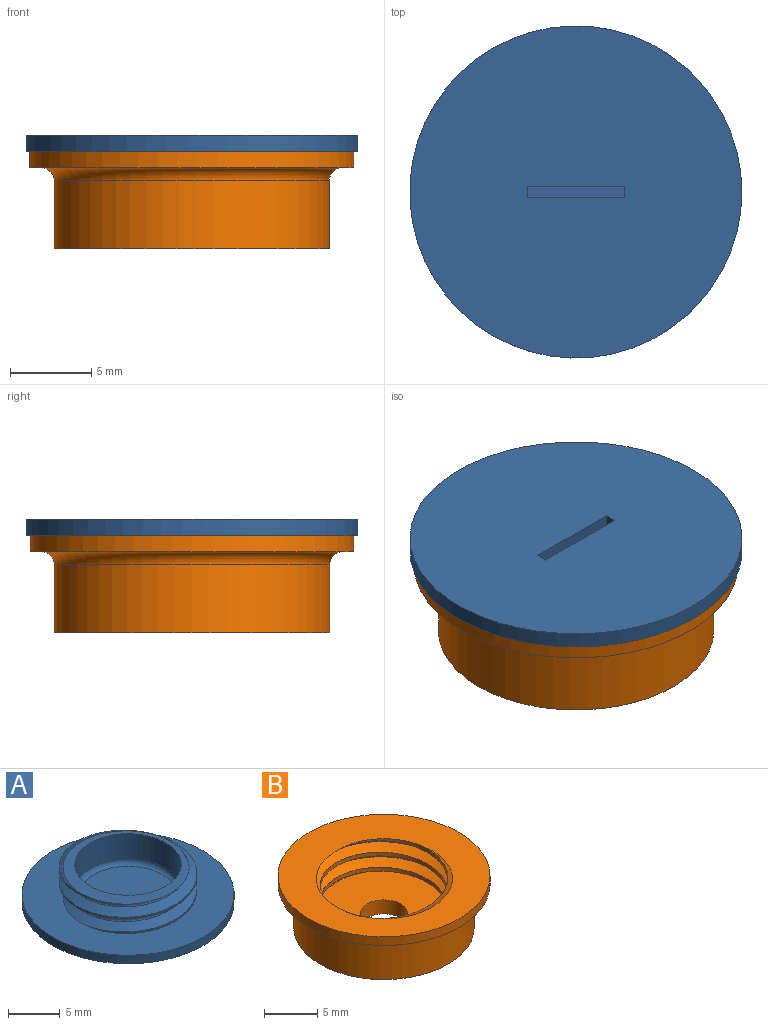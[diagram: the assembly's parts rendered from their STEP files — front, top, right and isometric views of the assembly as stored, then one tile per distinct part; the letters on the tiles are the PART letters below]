
ASSEMBLY  parts=2 mates=1
PART A: 16 faces, bbox 21x21x5.7 mm
  f0: plane 20.5x20.5mm, normal (0,0,-1), area 325.9mm2, adj f1,f11,f12,f13,f14
  f1: cylinder r=10.25mm len=20.5mm, axis (0,0,-1), area 64.4mm2, adj f0,f2
  f2: plane 20.99x20.99mm, normal (0,0,1), area 212.7mm2, adj f1,f4,f7,f8,f9
  f3: cylinder r=5.15mm len=10.3mm, axis (0,0,-1), area 97.1mm2, adj f5,f10
  f4: cylinder r=6.65mm len=13.3mm, axis (0,0,-1), area 18.3mm2, adj f2,f5,f8,f9
  f5: plane 12.77x12.71mm, normal (0,0,1), area 34.1mm2, adj f3,f4,f7,f8,f9
  f6: plane 9.3x9.3mm, normal (0,0,1), area 67.9mm2, adj f10
  f7: bspline ~13.17x11.41mm, area 34.7mm2, adj f2,f5,f8,f9
  f8: bspline ~15.36x13.3mm, area 85mm2, adj f2,f4,f5,f7
  f9: bspline ~15.36x13.3mm, area 85mm2, adj f2,f4,f5,f7
  f10: torus R=4.65mm, axis (0,0,1), area 24.5mm2, adj f3,f6
  f11: plane 0.8x0.7mm, normal (-1,0,0), area 0.6mm2, adj f0,f12,f14,f15
  f12: plane 6x0.8mm, normal (0,1,0), area 4.8mm2, adj f0,f11,f13,f15
  f13: plane 0.8x0.7mm, normal (1,0,0), area 0.6mm2, adj f0,f12,f14,f15
  f14: plane 6x0.8mm, normal (0,-1,0), area 4.8mm2, adj f0,f11,f13,f15
  f15: plane 6x0.7mm, normal (0,0,-1), area 4.2mm2, adj f11,f12,f13,f14
PART B: 12 faces, bbox 21.9x21.9x7.3 mm
  f0: plane 17x17mm, normal (0,0,-1), area 211.1mm2, adj f5,f6
  f1: plane 13.35x13.34mm, normal (0,0,1), area 115mm2, adj f6,f7,f8,f9,f10
  f2: plane 20.54x20.54mm, normal (0,0,1), area 183.3mm2, adj f3,f7,f8,f9,f10
  f3: cylinder r=10mm len=20mm, axis (0,0,-1), area 62.8mm2, adj f2,f4
  f4: plane 20x20mm, normal (0,0,-1), area 42.4mm2, adj f3,f11
  f5: cylinder r=8.5mm len=17mm, axis (0,0,-1), area 224.3mm2, adj f0,f11
  f6: cylinder r=2.25mm len=4.5mm, axis (0,0,-1), area 22.6mm2, adj f0,f1
  f7: bspline ~16.1x13.94mm, area 112.5mm2, adj f1,f2,f9,f10
  f8: bspline ~16.1x13.94mm, area 112.3mm2, adj f1,f2,f9,f10
  f9: bspline ~16.29x14.1mm, area 28.1mm2, adj f1,f2,f7,f8
  f10: cylinder r=6.03mm len=12.05mm, axis (0,0,1), area 41.4mm2, adj f1,f2,f7,f8
  f11: torus R=9.3mm, axis (0,0,-1), area 69.4mm2, adj f4,f5
PLACE A rot(axis=(1,0,0),180deg) t=(-6.89,-1.17,8.96)mm
PLACE B t=(-6.89,-1.17,1.96)mm fixed
MATE cylindrical B.f3 <-> A.f1  axis (0,0,1) through (-6.89,-1.17,7.96)mm
